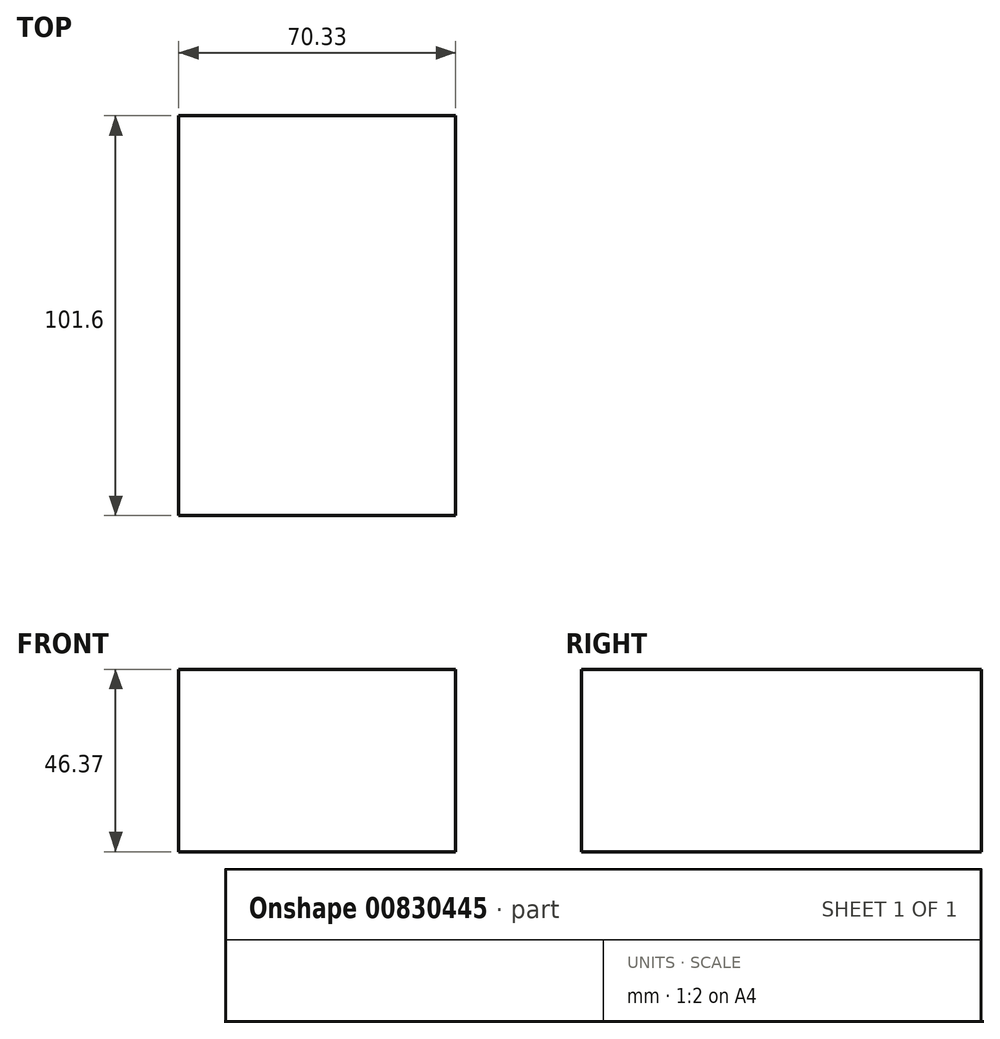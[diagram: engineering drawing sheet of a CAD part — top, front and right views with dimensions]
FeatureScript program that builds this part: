
annotation { "Feature Type Name" : "Feature", "Feature Type Description" : "" }
export const myFeature = defineFeature(function(context is Context, id is Id, definition is map)
    precondition{}
    {
        {
            var Q0;
            Q0=qCreatedBy(makeId("Front.planeOp"),FACE);
            var sketch = newSketch(context, id + "F0", { "sketchPlane" : qUnion([Q0])});
            skLineSegment(sketch, "E0.bottom", {"start": v(0, 46.37) * mm, "end": v(70.33, 46.37) * mm});
            skLineSegment(sketch, "E0.top", {"start": v(0, 0) * mm, "end": v(70.33, 0) * mm});
            skLineSegment(sketch, "E0.left", {"start": v(0, 46.37) * mm, "end": v(0, 0) * mm});
            skLineSegment(sketch, "E0.right", {"start": v(70.33, 46.37) * mm, "end": v(70.33, 0) * mm});
            skSolve(sketch);
        }
        {
            var Q0;
            Q0=makeQuery(id+"F0.imprint","IMPRINT",FACE,{"disambiguationData":[TD([[makeQuery(id+"F0.imprint","IMPRINT",EDGE,{"derivedFrom":sQuery(id+"F0.wireOp",EDGE,"E0.bottom")}),-1.0]])]});
            extrude(context, id + "F1", {"entities" : qUnion([Q0]), "depth" : 101.6 * mm, "offsetDistance" : 25.4 * mm});
        }
    });
